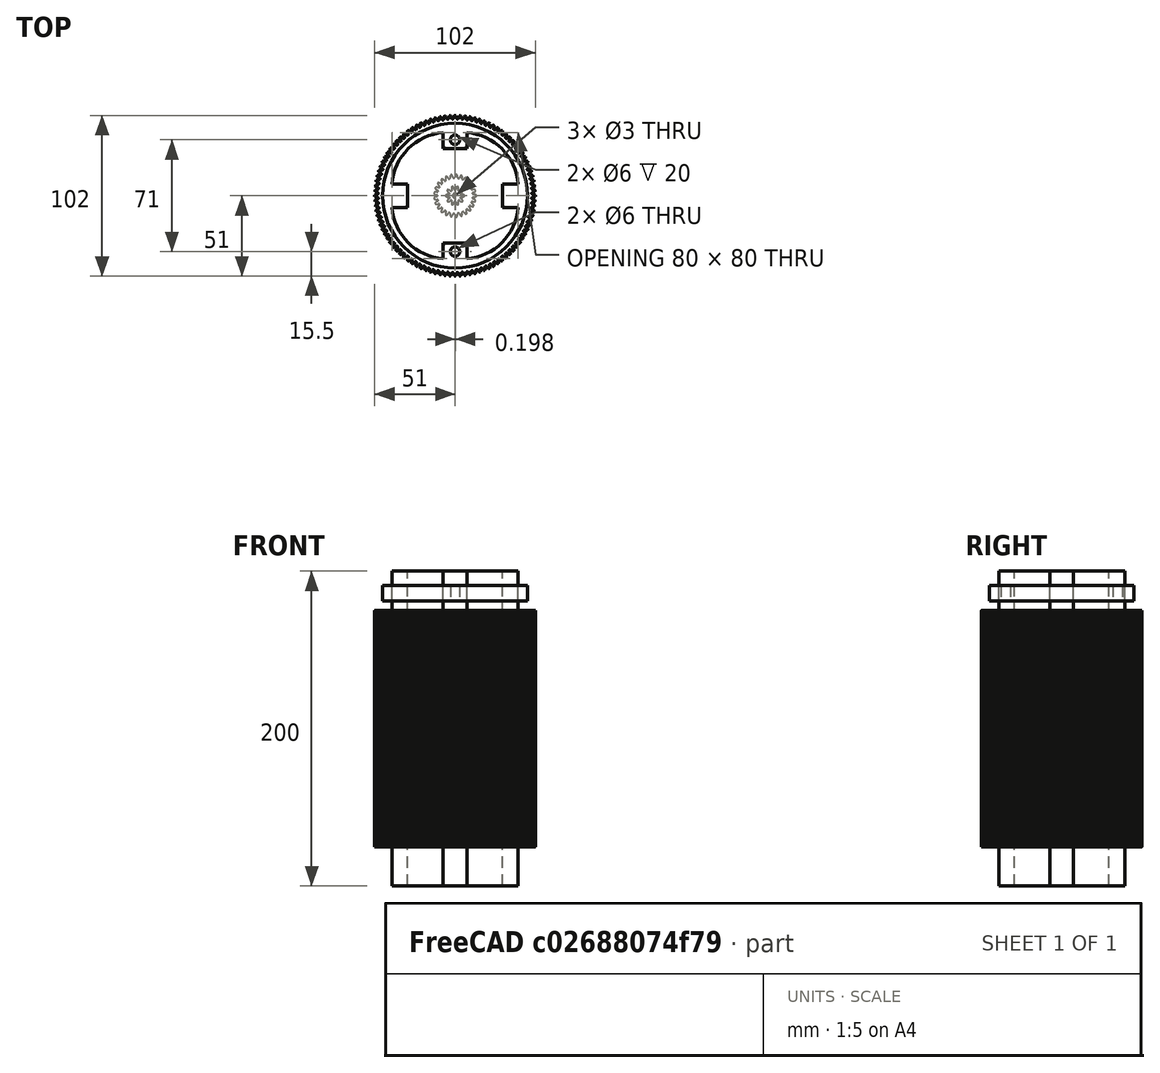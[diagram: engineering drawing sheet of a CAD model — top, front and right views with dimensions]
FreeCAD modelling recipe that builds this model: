
FCSTD DOCUMENT  (FreeCAD 0.20R29177 (Git))
Label: ball-mill
License: All rights reserved
LicenseURL: http://en.wikipedia.org/wiki/All_rights_reserved
objects: Sketcher::SketchObject×6, PartDesign::Body×6, PartDesign::Pad×5, PartDesign::Hole×5, App::Part×5, Mesh::Feature×5, Part::Part2DObjectPython×4, Part::Cylinder×2, PartDesign::FeatureBase×2, PartDesign::Boolean×2, PartDesign::Fillet×1
note: 44 computed .brp shape members not serialized (recipe doc carries the construction recipe); baked Part::Feature solids carry a one-line shape summary decoded from their .brp

FEATURE [Part::Part2DObjectPython] InvoluteGear  # Draft 2D object (typed FeaturePython)
  ExternalGear = true
  HighPrecision = true
  Modules = 1
  NumberOfTeeth = 100
  PressureAngle = 20
FEATURE [Sketcher::SketchObject] Sketch
  FullyConstrained = true
  MapMode = 5
  Support = -> [XY_Plane004]
  sketch-geometry (16):
    g0: LineSegment StartX=-40 StartY=7.5 StartZ=0 EndX=-30 EndY=7.5 EndZ=0
    g1: LineSegment StartX=-30 StartY=7.5 StartZ=0 EndX=-30 EndY=-7.5 EndZ=0
    g2: LineSegment StartX=-30 StartY=-7.5 StartZ=0 EndX=-40 EndY=-7.5 EndZ=0
    g3: LineSegment StartX=40 StartY=7.5 StartZ=0 EndX=30 EndY=7.5 EndZ=0
    g4: LineSegment StartX=30 StartY=7.5 StartZ=0 EndX=30 EndY=-7.5 EndZ=0
    g5: LineSegment StartX=30 StartY=-7.5 StartZ=0 EndX=40 EndY=-7.5 EndZ=0
    g6: LineSegment StartX=-7.5 StartY=-40 StartZ=0 EndX=-7.5 EndY=-30 EndZ=0
    g7: LineSegment StartX=-7.5 StartY=-30 StartZ=0 EndX=7.5 EndY=-30 EndZ=0
    g8: LineSegment StartX=7.5 StartY=-30 StartZ=0 EndX=7.5 EndY=-40 EndZ=0
    g9: LineSegment StartX=7.5 StartY=40 StartZ=0 EndX=7.5 EndY=30 EndZ=0
    g10: LineSegment StartX=7.5 StartY=30 StartZ=0 EndX=-7.5 EndY=30 EndZ=0
    g11: LineSegment StartX=-7.5 StartY=30 StartZ=0 EndX=-7.5 EndY=40 EndZ=0
    g12: ArcOfCircle CenterX=-5 CenterY=5 CenterZ=0 NormalX=0 NormalY=0 NormalZ=1 AngleXU=0 Radius=35.0892 StartAngle=1.6421 EndAngle=3.07029
    g13: ArcOfCircle CenterX=5 CenterY=5 CenterZ=0 NormalX=0 NormalY=0 NormalZ=1 AngleXU=0 Radius=35.0892 StartAngle=0.0713075 EndAngle=1.49949
    g14: ArcOfCircle CenterX=-5 CenterY=-5 CenterZ=0 NormalX=0 NormalY=0 NormalZ=1 AngleXU=0 Radius=35.0892 StartAngle=3.2129 EndAngle=4.64108
    g15: ArcOfCircle CenterX=5 CenterY=-5 CenterZ=0 NormalX=0 NormalY=0 NormalZ=1 AngleXU=0 Radius=35.0892 StartAngle=4.7837 EndAngle=6.21188
  constraints (52):
    c: Horizontal(g0)
    c: Coincident(g0,g1)
    c: Vertical(g1)
    c: Coincident(g1,g2)
    c: Horizontal(g2)
    c: Distance(g0,g1) = 15
    c: Distance(g0,g0) = 10
    c: Distance(g1,g2) = 10
    c: DistanceX(g1,g-1) = 30
    c: DistanceY(g1,g-1) = 7.5
    c: Horizontal(g3)
    c: Coincident(g4,g3)
    c: Vertical(g4)
    c: Coincident(g5,g4)
    c: Horizontal(g5)
    c: Distance(g3,g4) = 15
    c: Distance(g3,g3) = 10
    c: Distance(g4,g5) = 10
    c: DistanceX(g-1,g4) = 30
    c: DistanceY(g4,g-1) = 7.5
    c: Coincident(g7,g6)
    c: Coincident(g8,g7)
    c: Vertical(g8)
    c: Distance(g6,g6) = 10
    c: Distance(g7,g8) = 10
    c: Distance(g6,g7) = 15
    c: Parallel(g6,g8)
    c: Parallel(g7,g-1)
    c: DistanceX(g-1,g7) = 7.5
    c: Coincident(g9,g10)
    c: Coincident(g10,g11)
    c: Horizontal(g10)
    c: Vertical(g9)
    c: Vertical(g11)
    c: Distance(g10,g9) = 15
    c: Distance(g11,g10) = 10
    c: Distance(g9,g9) = 10
    c: DistanceX(g-1,g9) = 7.5
    c: DistanceY(g7,g-1) = 30
    c: DistanceY(g-1,g9) = 30
    c: Coincident(g12,g11)
    c: Coincident(g12,g0)
    c: DistanceX(g0,g12) = 25
    c: Coincident(g13,g9)
    c: Coincident(g13,g3)
    c: DistanceY(g13,g9) = 25
    c: Coincident(g14,g2)
    c: Coincident(g14,g6)
    c: DistanceY(g6,g14) = 25
    c: Coincident(g15,g8)
    c: Coincident(g15,g5)
    c: DistanceX(g15,g4) = 25
FEATURE [PartDesign::Pad] Pad001  label="inner hole pad"
  Direction = (0,0,1)
  Length = 200
  Length2 = 10
  Profile = -> Sketch
  ReferenceAxis = -> Sketch [N_Axis]
  Type = 0
FEATURE [PartDesign::Body] Body002  label="inner hole"
  Group = -> [Sketch,Pad001]
  Origin = -> Origin004
  Placement = pos=(0,0,-25) rot=(0,0,1;0rad)
  Tip = -> Pad001
FEATURE [Part::Cylinder] Cylinder  label="back cover"
  Angle = 360
  AttacherType = Attacher::AttachEngine3D
  FirstAngle = 0
  Height = 10
  Radius = 45
  SecondAngle = 0
FEATURE [PartDesign::FeatureBase] BaseFeature
  BaseFeature = -> Cylinder
FEATURE [PartDesign::Pad] Pad  label="container pad"
  BaseFeature = -> BaseFeature
  Direction = (0,0,1)
  Length = 150
  Length2 = 10
  Profile = -> InvoluteGear
  ReferenceAxis = -> InvoluteGear [N_Axis]
  Type = 0
FEATURE [PartDesign::Boolean] Boolean
  BaseFeature = -> Pad
  Group = -> [Body002]
  Type = 1
FEATURE [Part::Cylinder] Cylinder001  label="front cover"
  Angle = 360
  AttacherType = Attacher::AttachEngine3D
  FirstAngle = 0
  Height = 10
  Placement = pos=(0,0,150) rot=(0,0,1;0rad)
  Radius = 46
  SecondAngle = 0
FEATURE [PartDesign::FeatureBase] BaseFeature001
  BaseFeature = -> Cylinder001
FEATURE [Sketcher::SketchObject] Sketch001  label="screw holes"
  FullyConstrained = true
  MapMode = 5
  Placement = pos=(0,0,150) rot=(0,0,1;0rad)
  Support = -> [Boolean]
  sketch-geometry (2):
    g0: Circle CenterX=0 CenterY=35.5 CenterZ=0 NormalX=0 NormalY=0 NormalZ=1 AngleXU=0 Radius=3
    g1: Circle CenterX=0 CenterY=-35.5 CenterZ=0 NormalX=0 NormalY=0 NormalZ=1 AngleXU=0 Radius=3
  constraints (6):
    c: Diameter(g0) = 6
    c: DistanceY(g-1,g0) = 35.5
    c: DistanceX(g0,g-1) = 0
    c: DistanceY(g1,g-1) = 35.5
    c: DistanceX(g1,g-1) = 0
    c: Diameter(g1) = 6
FEATURE [PartDesign::Hole] Hole  label="top screw holes"
  BaseFeature = -> Boolean
  CustomThreadClearance = 0
  Depth = 20
  DepthType = 0
  Diameter = 6
  DrillForDepth = false
  DrillPoint = 0
  DrillPointAngle = 118
  HoleCutCountersinkAngle = 90
  HoleCutCustomValues = false
  HoleCutDepth = 0
  HoleCutDiameter = 6.1
  HoleCutType = 0
  ModelThread = false
  Profile = -> Sketch001
  Tapered = false
  TaperedAngle = 90
  ThreadClass = 0
  ThreadDepth = 20
  ThreadDepthType = 0
  ThreadDirection = 0
  ThreadFit = 0
  ThreadSize = 0
  ThreadType = 0
  Threaded = false
  UseCustomThreadClearance = false
FEATURE [Sketcher::SketchObject] Sketch002  label="lid screw holes"
  FullyConstrained = true
  MapMode = 5
  Placement = pos=(0,0,10) rot=(0,0,1;0rad)
  Support = -> [BaseFeature001]
  sketch-geometry (2):
    g0: Circle CenterX=0 CenterY=35.5 CenterZ=0 NormalX=0 NormalY=0 NormalZ=1 AngleXU=0 Radius=3
    g1: Circle CenterX=0 CenterY=-35.5 CenterZ=0 NormalX=0 NormalY=0 NormalZ=1 AngleXU=0 Radius=3
  constraints (6):
    c: DistanceY(g-1,g0) = 35.5
    c: DistanceX(g0,g-1) = 0
    c: Diameter(g0) = 6
    c: DistanceX(g-1,g1) = 0
    c: DistanceY(g1,g-1) = 35.5
    c: Diameter(g1) = 6
FEATURE [PartDesign::Hole] Hole001  label="lid holes"
  BaseFeature = -> BaseFeature001
  CustomThreadClearance = 0
  Depth = 11
  DepthType = 0
  Diameter = 6
  DrillForDepth = false
  DrillPoint = 0
  DrillPointAngle = 118
  HoleCutCountersinkAngle = 90
  HoleCutCustomValues = false
  HoleCutDepth = 0
  HoleCutDiameter = 6.1
  HoleCutType = 0
  ModelThread = false
  Profile = -> Sketch002
  Tapered = false
  TaperedAngle = 90
  ThreadClass = 0
  ThreadDepth = 11
  ThreadDepthType = 0
  ThreadDirection = 0
  ThreadFit = 0
  ThreadSize = 0
  ThreadType = 0
  Threaded = false
  UseCustomThreadClearance = false
FEATURE [PartDesign::Body] Body003  label="lid body"
  BaseFeature = -> Cylinder001
  Group = -> [BaseFeature001,Sketch002,Hole001]
  Origin = -> Origin006
  Placement = pos=(0,0,156) rot=(0,0,1;0rad)
  Tip = -> Hole001
FEATURE [App::Part] Part002  label="container lid"
  Group = -> [Body003,Cylinder001]
  Origin = -> Origin005
FEATURE [PartDesign::Boolean] Boolean001  label="fuse with back cover"
  BaseFeature = -> Hole
  Group = -> [Cylinder]
  Type = 0
FEATURE [PartDesign::Fillet] Fillet  label="inner obstacle fillet"
  Base = -> Boolean001 [Edge2441,Edge2438,Edge2447,Edge2451,Edge2463,Edge2467,Edge2457,Edge2453]
  BaseFeature = -> Boolean001
  Radius = 3
  SupportTransform = false
  UseAllEdges = false
FEATURE [PartDesign::Body] Body
  BaseFeature = -> Cylinder
  Group = -> [BaseFeature,InvoluteGear,Pad,Boolean,Sketch001,Hole,Boolean001,Fillet]
  Origin = -> Origin001
  Tip = -> Fillet
FEATURE [App::Part] Part  label="container"
  Group = -> [Body]
  Origin = -> Origin
FEATURE [Mesh::Feature] Mesh  label="container (Meshed)"
FEATURE [Mesh::Feature] Mesh001  label="container lid (Meshed)"
FEATURE [Part::Part2DObjectPython] InvoluteGear001  label="motor gear001"  # Draft 2D object (typed FeaturePython)
  ExternalGear = true
  HighPrecision = true
  Modules = 1
  NumberOfTeeth = 10
  PressureAngle = 20
FEATURE [PartDesign::Pad] Pad002
  Direction = (0,0,1)
  Length = 10
  Length2 = 10
  Profile = -> InvoluteGear001
  ReferenceAxis = -> InvoluteGear001 [N_Axis]
  Type = 0
FEATURE [Sketcher::SketchObject] Sketch003  label="motor gear hole"
  FullyConstrained = false
  MapMode = 5
  Placement = pos=(0,0,10) rot=(0,0,1;0rad)
  Support = -> [Pad002]
  sketch-geometry (1):
    g0: Circle CenterX=0.198008 CenterY=0 CenterZ=0 NormalX=0 NormalY=0 NormalZ=1 AngleXU=0 Radius=1.5
  constraints (2):
    c: PointOnObject(g0,g-1)
    c: Diameter(g0) = 3
FEATURE [PartDesign::Hole] Hole002
  BaseFeature = -> Pad002
  CustomThreadClearance = 0
  Depth = 25
  DepthType = 0
  Diameter = 3
  DrillForDepth = false
  DrillPoint = 1
  DrillPointAngle = 118
  HoleCutCountersinkAngle = 90
  HoleCutCustomValues = false
  HoleCutDepth = 0
  HoleCutDiameter = 6.1
  HoleCutType = 0
  ModelThread = false
  Profile = -> Sketch003
  Tapered = false
  TaperedAngle = 90
  ThreadClass = 0
  ThreadDepth = 25
  ThreadDepthType = 0
  ThreadDirection = 0
  ThreadFit = 0
  ThreadSize = 0
  ThreadType = 0
  Threaded = false
  UseCustomThreadClearance = false
FEATURE [PartDesign::Body] Body004  label="motor gear body"
  Group = -> [InvoluteGear001,Pad002,Sketch003,Hole002]
  Origin = -> Origin008
  Tip = -> Hole002
FEATURE [App::Part] Part003  label="motor gear"
  Group = -> [Body004]
  Origin = -> Origin007
FEATURE [Part::Part2DObjectPython] InvoluteGear002  # Draft 2D object (typed FeaturePython)
  ExternalGear = true
  HighPrecision = true
  Modules = 1
  NumberOfTeeth = 100
  PressureAngle = 20
FEATURE [PartDesign::Pad] Pad003
  Direction = (0,0,1)
  Length = 20
  Length2 = 10
  Profile = -> InvoluteGear002
  ReferenceAxis = -> InvoluteGear002 [N_Axis]
  Type = 0
FEATURE [Sketcher::SketchObject] Sketch004  label="shaft gear hole"
  FullyConstrained = true
  MapMode = 5
  Placement = pos=(0,0,20) rot=(0,0,1;0rad)
  Support = -> [Pad003]
  sketch-geometry (1):
    g0: Circle CenterX=0 CenterY=0 CenterZ=0 NormalX=0 NormalY=0 NormalZ=1 AngleXU=0 Radius=1.5
  constraints (2):
    c: Coincident(g0,g-1)
    c: Diameter(g0) = 3
FEATURE [PartDesign::Hole] Hole003
  BaseFeature = -> Pad003
  CustomThreadClearance = 0
  Depth = 25
  DepthType = 0
  Diameter = 3
  DrillForDepth = false
  DrillPoint = 1
  DrillPointAngle = 118
  HoleCutCountersinkAngle = 90
  HoleCutCustomValues = false
  HoleCutDepth = 0
  HoleCutDiameter = 6.1
  HoleCutType = 0
  ModelThread = false
  Profile = -> Sketch004
  Tapered = false
  TaperedAngle = 90
  ThreadClass = 0
  ThreadDepth = 25
  ThreadDepthType = 0
  ThreadDirection = 0
  ThreadFit = 0
  ThreadSize = 0
  ThreadType = 0
  Threaded = false
  UseCustomThreadClearance = false
FEATURE [PartDesign::Body] Body005  label="shaft gear body"
  Group = -> [InvoluteGear002,Pad003,Sketch004,Hole003]
  Origin = -> Origin010
  Tip = -> Hole003
FEATURE [App::Part] Part004  label="shaft gear"
  Group = -> [Body005]
  Origin = -> Origin009
FEATURE [Part::Part2DObjectPython] InvoluteGear003  # Draft 2D object (typed FeaturePython)
  ExternalGear = true
  HighPrecision = true
  Modules = 1
  NumberOfTeeth = 25
  PressureAngle = 20
FEATURE [PartDesign::Pad] Pad004
  Direction = (0,0,1)
  Length = 30
  Length2 = 10
  Profile = -> InvoluteGear003
  ReferenceAxis = -> InvoluteGear003 [N_Axis]
  Type = 0
FEATURE [Sketcher::SketchObject] Sketch005  label="drive gear hole"
  FullyConstrained = true
  MapMode = 5
  Placement = pos=(0,0,30) rot=(0,0,1;0rad)
  Support = -> [Pad004]
  sketch-geometry (1):
    g0: Circle CenterX=0 CenterY=0 CenterZ=0 NormalX=0 NormalY=0 NormalZ=1 AngleXU=0 Radius=1.5
  constraints (2):
    c: Coincident(g0,g-1)
    c: Diameter(g0) = 3
FEATURE [PartDesign::Hole] Hole004
  BaseFeature = -> Pad004
  CustomThreadClearance = 0
  Depth = 50
  DepthType = 0
  Diameter = 3
  DrillForDepth = false
  DrillPoint = 1
  DrillPointAngle = 118
  HoleCutCountersinkAngle = 90
  HoleCutCustomValues = false
  HoleCutDepth = 0
  HoleCutDiameter = 6.1
  HoleCutType = 0
  ModelThread = false
  Profile = -> Sketch005
  Tapered = false
  TaperedAngle = 90
  ThreadClass = 0
  ThreadDepth = 50
  ThreadDepthType = 0
  ThreadDirection = 0
  ThreadFit = 0
  ThreadSize = 0
  ThreadType = 0
  Threaded = false
  UseCustomThreadClearance = false
FEATURE [PartDesign::Body] Body006  label="drive gear body"
  Group = -> [InvoluteGear003,Pad004,Sketch005,Hole004]
  Origin = -> Origin012
  Tip = -> Hole004
FEATURE [App::Part] Part005  label="drive gear"
  Group = -> [Body006]
  Origin = -> Origin011
FEATURE [Mesh::Feature] Mesh002  label="drive gear (Meshed)"
FEATURE [Mesh::Feature] Mesh003  label="shaft gear (Meshed)"
FEATURE [Mesh::Feature] Mesh004  label="motor gear (Meshed)"
